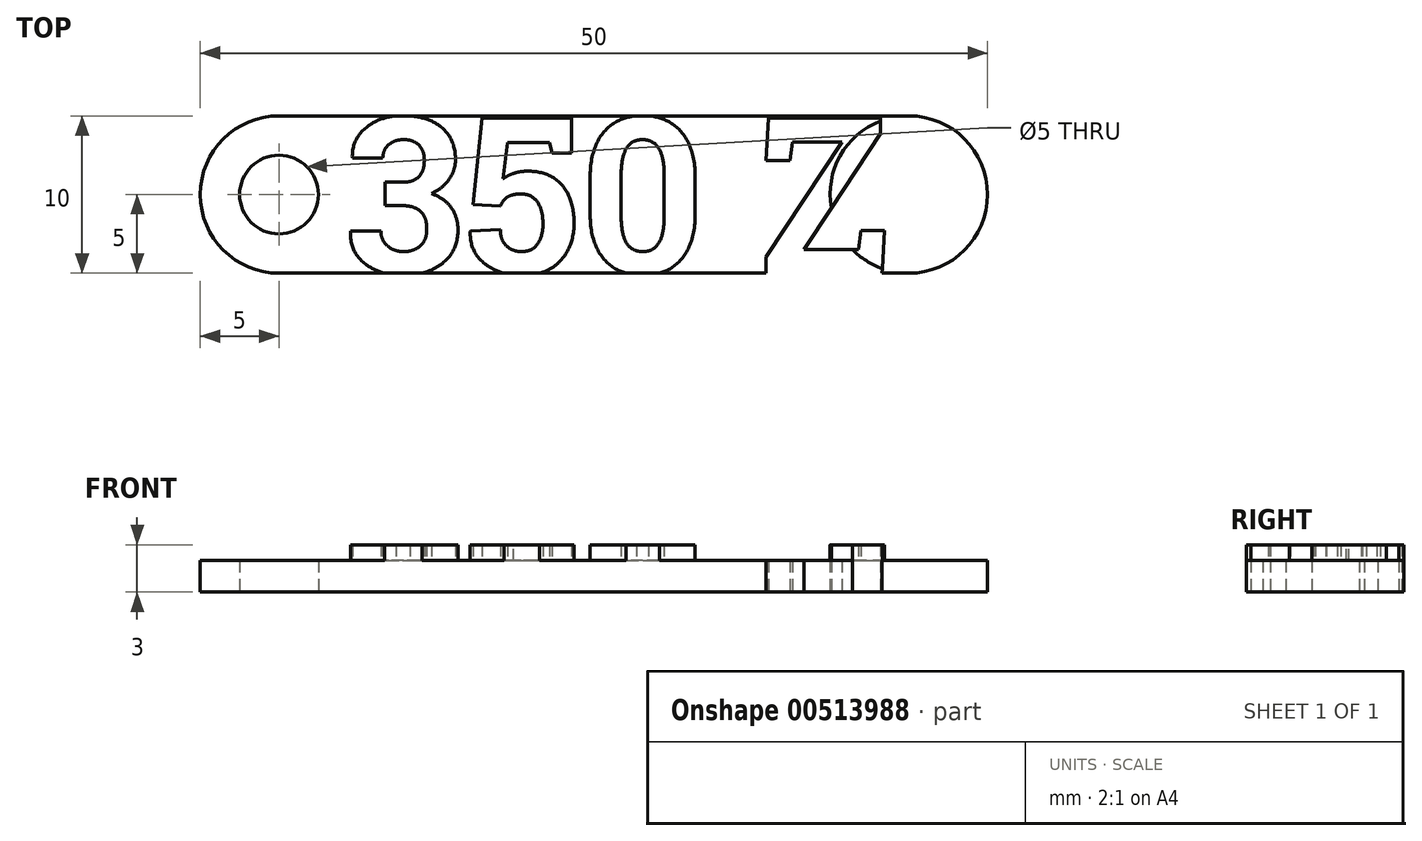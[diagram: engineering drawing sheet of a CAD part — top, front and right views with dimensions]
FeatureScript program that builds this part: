
annotation { "Feature Type Name" : "Feature", "Feature Type Description" : "" }
export const myFeature = defineFeature(function(context is Context, id is Id, definition is map)
    precondition{}
    {
        {
            var Q0;
            Q0=qCreatedBy(makeId("Top.planeOp"),FACE);
            var sketch = newSketch(context, id + "F0", { "sketchPlane" : qUnion([Q0])});
            skCircle(sketch, "E0", {"center": v(-20, 0) * mm, "radius": 2.5 * mm});
            skCircle(sketch, "E1", {"center": v(-20, 0) * mm, "radius": 5 * mm});
            skCircle(sketch, "E2", {"center": v(20, 0) * mm, "radius": 5 * mm});
            skLineSegment(sketch, "E3", {"start": v(-20, 5) * mm, "end": v(20, 5) * mm});
            skLineSegment(sketch, "E4", {"start": v(-20, -5) * mm, "end": v(20, -5) * mm});
            skText(sketch, "E5", { "text": "350 Z", "fontName": "RobotoSlab-Bold.ttf"});
            const initialGuessF0  = {"E5": [-0.01585, -0.005, 1, 0, 0.01]};
            skSetInitialGuess(sketch, initialGuessF0);
            skSolve(sketch);
        }
        {
            var Q0;
            {var subQ0=sQuery(id+"F0.wireOp",EDGE,"6bbc4e0a-0422-471a-a432-42bab2623723.sketch_text.stroke-9");Q0=makeQuery(id+"F0.imprint","IMPRINT",FACE,{"disambiguationData":[TD([[makeQuery(id+"F0.imprint","IMPRINT",EDGE,{"derivedFrom":subQ0}),1.0]])]});}
            var Q1;
            Q1=makeQuery(id+"F0.imprint","IMPRINT",FACE,{"disambiguationData":[TD([[makeQuery(id+"F0.imprint","IMPRINT",EDGE,{"derivedFrom":sQuery(id+"F0.wireOp",EDGE,"6bbc4e0a-0422-471a-a432-42bab2623723.sketch_text.stroke-0")}),1.0]])]});
            var Q2;
            Q2=makeQuery(id+"F0.imprint","IMPRINT",FACE,{"disambiguationData":[TD([[makeQuery(id+"F0.imprint","IMPRINT",EDGE,{"derivedFrom":sQuery(id+"F0.wireOp",EDGE,"6bbc4e0a-0422-471a-a432-42bab2623723.sketch_text.stroke-55")}),1.0]])]});
            var Q3;
            {var subQ5=sQuery(id+"F0.wireOp",EDGE,"6bbc4e0a-0422-471a-a432-42bab2623723.sketch_text.stroke-47");Q3=makeQuery(id+"F0.imprint","IMPRINT",FACE,{"disambiguationData":[TD([[makeQuery(id+"F0.imprint","IMPRINT",EDGE,{"derivedFrom":subQ5}),1.0]])]});}
            var Q4;
            {var subQ0=sQuery(id+"F0.wireOp",EDGE,"6bbc4e0a-0422-471a-a432-42bab2623723.sketch_text.stroke-71");Q4=makeQuery(id+"F0.imprint","IMPRINT",FACE,{"disambiguationData":[TD([[makeQuery(id+"F0.imprint","IMPRINT",EDGE,{"derivedFrom":subQ0}),1.0]])]});}
            var Q5;
            {var subQ0=sQuery(id+"F0.wireOp",EDGE,"E2");var subQ1=makeQuery(id+"F0.imprint","INTERSECT",VERTEX,{"derivedFrom":[subQ0,sQuery(id+"F0.wireOp",EDGE,"E3")]});Q5=makeQuery(id+"F0.imprint","IMPRINT",FACE,{"disambiguationData":[TD([[makeQuery(id+"F0.imprint","IMPRINT",EDGE,{"disambiguationData":[TD([[subQ1,-1.0]])],"derivedFrom":subQ0}),1.0]])]});}
            var Q6;
            Q6=makeQuery(id+"F0.imprint","IMPRINT",FACE,{"disambiguationData":[TD([[makeQuery(id+"F0.imprint","IMPRINT",EDGE,{"derivedFrom":sQuery(id+"F0.wireOp",EDGE,"E0")}),-1.0]])]});
            var Q7;
            Q7=makeQuery(id+"F0.imprint","IMPRINT",FACE,{"disambiguationData":[TD([[makeQuery(id+"F0.imprint","IMPRINT",EDGE,{"derivedFrom":sQuery(id+"F0.wireOp",EDGE,"6bbc4e0a-0422-471a-a432-42bab2623723.sketch_text.stroke-0")}),-1.0]])]});
            var Q8;
            Q8=makeQuery(id+"F0.imprint","IMPRINT",FACE,{"disambiguationData":[TD([[makeQuery(id+"F0.imprint","IMPRINT",EDGE,{"derivedFrom":sQuery(id+"F0.wireOp",EDGE,"6bbc4e0a-0422-471a-a432-42bab2623723.sketch_text.stroke-28")}),-1.0]])]});
            var Q9;
            {var subQ13=sQuery(id+"F0.wireOp",EDGE,"6bbc4e0a-0422-471a-a432-42bab2623723.sketch_text.stroke-47");Q9=makeQuery(id+"F0.imprint","IMPRINT",FACE,{"disambiguationData":[TD([[makeQuery(id+"F0.imprint","IMPRINT",EDGE,{"derivedFrom":subQ13}),-1.0]])]});}
            var Q10;
            Q10=makeQuery(id+"F0.imprint","IMPRINT",FACE,{"disambiguationData":[TD([[makeQuery(id+"F0.imprint","IMPRINT",EDGE,{"derivedFrom":sQuery(id+"F0.wireOp",EDGE,"6bbc4e0a-0422-471a-a432-42bab2623723.sketch_text.stroke-63")}),-1.0]])]});
            var Q11;
            {var subQ0=sQuery(id+"F0.wireOp",EDGE,"6bbc4e0a-0422-471a-a432-42bab2623723.sketch_text.stroke-70");var subQ1=sQuery(id+"F0.wireOp",EDGE,"E2");var subQ2=makeQuery(id+"F0.imprint","INTERSECT",VERTEX,{"disambiguationData":[OD(0.0)],"derivedFrom":[subQ1,subQ0]});Q11=makeQuery(id+"F0.imprint","IMPRINT",FACE,{"disambiguationData":[TD([[makeQuery(id+"F0.imprint","IMPRINT",EDGE,{"disambiguationData":[TD([[subQ2,-1.0]])],"derivedFrom":subQ1}),1.0]])]});}
            var Q12;
            {var subQ18=sQuery(id+"F0.wireOp",EDGE,"E5.sketch_text.stroke-12");Q12=makeQuery(id+"F0.imprint","IMPRINT",FACE,{"disambiguationData":[TD([[makeQuery(id+"F0.imprint","IMPRINT",EDGE,{"derivedFrom":subQ18}),1.0]])]});}
            var Q13;
            Q13=makeQuery(id+"F0.imprint","IMPRINT",FACE,{"disambiguationData":[TD([[makeQuery(id+"F0.imprint","IMPRINT",EDGE,{"derivedFrom":sQuery(id+"F0.wireOp",EDGE,"E5.sketch_text.stroke-0")}),1.0]])]});
            var Q14;
            Q14=makeQuery(id+"F0.imprint","IMPRINT",FACE,{"disambiguationData":[TD([[makeQuery(id+"F0.imprint","IMPRINT",EDGE,{"derivedFrom":sQuery(id+"F0.wireOp",EDGE,"E5.sketch_text.stroke-0")}),-1.0]])]});
            var Q15;
            Q15=makeQuery(id+"F0.imprint","IMPRINT",FACE,{"disambiguationData":[TD([[makeQuery(id+"F0.imprint","IMPRINT",EDGE,{"derivedFrom":sQuery(id+"F0.wireOp",EDGE,"E5.sketch_text.stroke-31")}),-1.0]])]});
            var Q16;
            {var subQ13=sQuery(id+"F0.wireOp",EDGE,"E5.sketch_text.stroke-57");Q16=makeQuery(id+"F0.imprint","IMPRINT",FACE,{"disambiguationData":[TD([[makeQuery(id+"F0.imprint","IMPRINT",EDGE,{"derivedFrom":subQ13}),-1.0]])]});}
            var Q17;
            Q17=makeQuery(id+"F0.imprint","IMPRINT",FACE,{"disambiguationData":[TD([[makeQuery(id+"F0.imprint","IMPRINT",EDGE,{"derivedFrom":sQuery(id+"F0.wireOp",EDGE,"E5.sketch_text.stroke-67")}),1.0]])]});
            var Q18;
            {var subQ7=sQuery(id+"F0.wireOp",EDGE,"E5.sketch_text.stroke-57");Q18=makeQuery(id+"F0.imprint","IMPRINT",FACE,{"disambiguationData":[TD([[makeQuery(id+"F0.imprint","IMPRINT",EDGE,{"derivedFrom":subQ7}),1.0]])]});}
            var Q19;
            {var subQ5=sQuery(id+"F0.wireOp",EDGE,"E5.sketch_text.stroke-83");Q19=makeQuery(id+"F0.imprint","IMPRINT",FACE,{"disambiguationData":[TD([[makeQuery(id+"F0.imprint","IMPRINT",EDGE,{"derivedFrom":subQ5}),-1.0]])]});}
            var Q20;
            {var subQ0=sQuery(id+"F0.wireOp",EDGE,"E5.sketch_text.stroke-77");var subQ1=sQuery(id+"F0.wireOp",EDGE,"E2");var subQ2=makeQuery(id+"F0.imprint","INTERSECT",VERTEX,{"derivedFrom":[subQ1,subQ0]});Q20=makeQuery(id+"F0.imprint","IMPRINT",FACE,{"disambiguationData":[TD([[makeQuery(id+"F0.imprint","IMPRINT",EDGE,{"disambiguationData":[TD([[subQ2,-1.0]])],"derivedFrom":subQ1}),1.0]])]});}
            var Q21;
            {var subQ0=sQuery(id+"F0.wireOp",EDGE,"E5.sketch_text.stroke-78");var subQ1=sQuery(id+"F0.wireOp",EDGE,"E2");var subQ2=makeQuery(id+"F0.imprint","INTERSECT",VERTEX,{"derivedFrom":[subQ1,subQ0]});Q21=makeQuery(id+"F0.imprint","IMPRINT",FACE,{"disambiguationData":[TD([[makeQuery(id+"F0.imprint","IMPRINT",EDGE,{"disambiguationData":[TD([[subQ2,-1.0]])],"derivedFrom":subQ1}),-1.0]])]});}
            var Q22;
            {var subQ0=sQuery(id+"F0.wireOp",EDGE,"E5.sketch_text.stroke-80");Q22=makeQuery(id+"F0.imprint","IMPRINT",FACE,{"disambiguationData":[TD([[makeQuery(id+"F0.imprint","IMPRINT",EDGE,{"derivedFrom":subQ0}),-1.0]])]});}
            var Q23;
            {var subQ0=sQuery(id+"F0.wireOp",EDGE,"E4");var subQ1=sQuery(id+"F0.wireOp",EDGE,"E2");var subQ2=makeQuery(id+"F0.imprint","INTERSECT",VERTEX,{"derivedFrom":[subQ1,subQ0]});Q23=makeQuery(id+"F0.imprint","IMPRINT",FACE,{"disambiguationData":[TD([[makeQuery(id+"F0.imprint","IMPRINT",EDGE,{"disambiguationData":[TD([[subQ2,1.0]])],"derivedFrom":subQ1}),-1.0]])]});}
            extrude(context, id + "F1", {"entities" : qUnion([Q0, Q1, Q2, Q3, Q4, Q5, Q6, Q7, Q8, Q9, Q10, Q11, Q12, Q13, Q14, Q15, Q16, Q17, Q18, Q19, Q20, Q21, Q22, Q23]), "depth" : 2 * mm, "offsetDistance" : 25 * mm});
        }
        {
            var Q0;
            Q0=makeQuery(id+"F0.imprint","IMPRINT",FACE,{"disambiguationData":[TD([[makeQuery(id+"F0.imprint","IMPRINT",EDGE,{"derivedFrom":sQuery(id+"F0.wireOp",EDGE,"E5.sketch_text.stroke-0")}),-1.0]])]});
            var Q1;
            Q1=makeQuery(id+"F0.imprint","IMPRINT",FACE,{"disambiguationData":[TD([[makeQuery(id+"F0.imprint","IMPRINT",EDGE,{"derivedFrom":sQuery(id+"F0.wireOp",EDGE,"E5.sketch_text.stroke-31")}),-1.0]])]});
            var Q2;
            {var subQ13=sQuery(id+"F0.wireOp",EDGE,"E5.sketch_text.stroke-57");Q2=makeQuery(id+"F0.imprint","IMPRINT",FACE,{"disambiguationData":[TD([[makeQuery(id+"F0.imprint","IMPRINT",EDGE,{"derivedFrom":subQ13}),-1.0]])]});}
            var Q3;
            {var subQ5=sQuery(id+"F0.wireOp",EDGE,"E5.sketch_text.stroke-83");Q3=makeQuery(id+"F0.imprint","IMPRINT",FACE,{"disambiguationData":[TD([[makeQuery(id+"F0.imprint","IMPRINT",EDGE,{"derivedFrom":subQ5}),-1.0]])]});}
            var Q4;
            {var subQ0=sQuery(id+"F0.wireOp",EDGE,"E5.sketch_text.stroke-77");var subQ1=sQuery(id+"F0.wireOp",EDGE,"E2");var subQ2=makeQuery(id+"F0.imprint","INTERSECT",VERTEX,{"derivedFrom":[subQ1,subQ0]});Q4=makeQuery(id+"F0.imprint","IMPRINT",FACE,{"disambiguationData":[TD([[makeQuery(id+"F0.imprint","IMPRINT",EDGE,{"disambiguationData":[TD([[subQ2,-1.0]])],"derivedFrom":subQ1}),1.0]])]});}
            var Q5;
            {var subQ0=sQuery(id+"F0.wireOp",EDGE,"E5.sketch_text.stroke-80");Q5=makeQuery(id+"F0.imprint","IMPRINT",FACE,{"disambiguationData":[TD([[makeQuery(id+"F0.imprint","IMPRINT",EDGE,{"derivedFrom":subQ0}),-1.0]])]});}
            extrude(context, id + "F2", {"entities" : qUnion([Q0, Q1, Q2, Q3, Q4, Q5]), "operationType" : NewBodyOperationType.ADD, "depth" : 3 * mm, "offsetDistance" : 25 * mm});
        }
    });
